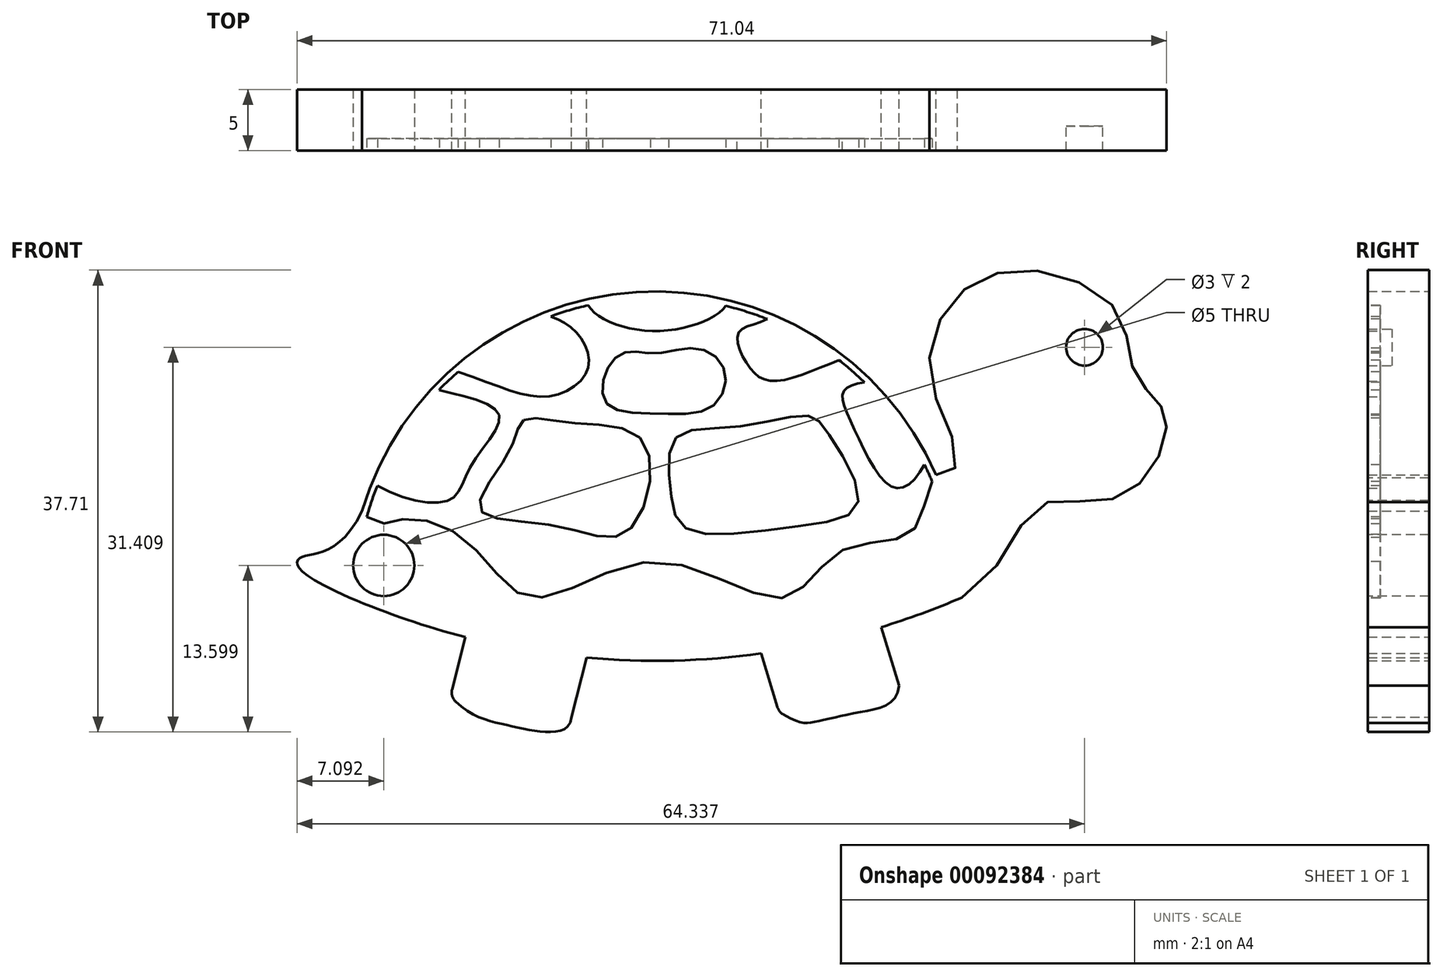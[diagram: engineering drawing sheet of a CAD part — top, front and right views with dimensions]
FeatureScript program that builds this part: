
annotation { "Feature Type Name" : "Feature", "Feature Type Description" : "" }
export const myFeature = defineFeature(function(context is Context, id is Id, definition is map)
    precondition{}
    {
        {
            var Q0;
            Q0=qCreatedBy(makeId("Front.planeOp"),FACE);
            var sketch = newSketch(context, id + "F0", { "sketchPlane" : qUnion([Q0])});
            skArc(sketch, "E0", {"start": v(25, 0) * mm, "mid": v(0, 25) * mm, "end": v(-25, 0) * mm});
            skArc(sketch, "E1", {"start": v(-25, 0) * mm, "mid": v(0, -5.16) * mm, "end": v(25, 0) * mm});
            skPoint(sketch, "E1.first.point", {"position": v(-25, 0) * mm});
            skPoint(sketch, "E1.second.point", {"position": v(25, 0) * mm});
            skArc(sketch, "E2", {"start": v(-22.9, 10.03) * mm, "mid": v(0, 4.84) * mm, "end": v(22.9, 10.03) * mm});
            skPoint(sketch, "E3.endSnap0", {"position": v(0, -5.16) * mm});
            skLineSegment(sketch, "E4", {"start": v(0, -5.16) * mm, "end": v(0, 14.84) * mm, "construction": true});
            skFitSpline(sketch, "E5.MirrorCS", {"points": [v(-22.9, 10.03) * mm, v(-28.86, 3.32) * mm, v(-25, 0) * mm], "startDerivative": vector(-9.95, -35.87) * mm, "endDerivative": vector(32.47, -14) * mm});
            skFitSpline(sketch, "E6", {"points": [v(22.9, 10.03) * mm, v(24.59, 11) * mm, v(22.49, 17.7) * mm, v(24.57, 24.55) * mm, v(30.78, 26.71) * mm, v(37.75, 23.3) * mm, v(39.05, 18.6) * mm, v(40.89, 16.14) * mm, v(41.74, 14.23) * mm, v(40.2, 10.04) * mm, v(36.08, 7.82) * mm, v(31.15, 7.38) * mm, v(25, 0) * mm], "startDerivative": vector(45.76, -39.88) * mm, "endDerivative": vector(-83.83, -36.13) * mm});
            skCircle(sketch, "E7", {"center": v(35.04, 20.44) * mm, "radius": 1.5 * mm});
            skArc(sketch, "E8", {"start": v(-24.41, 5.39) * mm, "mid": v(0, 0) * mm, "end": v(24.41, 5.39) * mm});
            skLineSegment(sketch, "E9", {"start": v(-15.53, -3.22) * mm, "end": v(-16.76, -8.07) * mm});
            skLineSegment(sketch, "E10", {"start": v(-6.87, -9.75) * mm, "end": v(-5.64, -4.9) * mm});
            skLineSegment(sketch, "E11", {"start": v(8.62, -4.57) * mm, "end": v(10.08, -9.35) * mm});
            skLineSegment(sketch, "E12", {"start": v(19.88, -7.2) * mm, "end": v(18.42, -2.41) * mm});
            skFitSpline(sketch, "E13", {"points": [v(-16.76, -8.07) * mm, v(-12.38, -10.35) * mm, v(-8.68, -10.97) * mm, v(-6.87, -9.75) * mm], "startDerivative": vector(11.77, -12.71) * mm, "endDerivative": vector(1.49, 11.94) * mm});
            skFitSpline(sketch, "E14", {"points": [v(10.08, -9.35) * mm, v(12.84, -10.18) * mm, v(16.55, -9.38) * mm, v(19.88, -7.2) * mm], "startDerivative": vector(16.48, -9.39) * mm, "endDerivative": vector(1.06, 14.58) * mm});
            skSolve(sketch);
        }
        {
            var Q0;
            Q0 = qSketchRegion(id + "F0", true);
            extrude(context, id + "F1", {"entities" : qUnion([Q0]), "depth" : 5 * mm});
        }
        {
            var Q0;
            Q0=makeQuery(id+"F1.opExtrude","CAP_FACE",FACE,{"disambiguationData":[OSD([sQuery(id+"F0.wireOp",EDGE,"E0"),sQuery(id+"F0.wireOp",EDGE,"E1"),sQuery(id+"F0.wireOp",EDGE,"E5.MirrorCS"),sQuery(id+"F0.wireOp",EDGE,"E6"),sQuery(id+"F0.wireOp",EDGE,"E7")])],"isStart":false});
            var sketch = newSketch(context, id + "F2", { "sketchPlane" : qUnion([Q0])});
            skFitSpline(sketch, "E15", {"points": [v(-5.68, 24.35) * mm, v(0, 21.77) * mm, v(5.98, 24.27) * mm], "startDerivative": vector(1.3, -8.7) * mm, "endDerivative": vector(2.25, 7.66) * mm});
            skFitSpline(sketch, "E16", {"points": [v(-16.68, 18.62) * mm, v(-8.69, 16.45) * mm, v(-5.54, 18.67) * mm, v(-6.45, 21.62) * mm, v(-9.3, 23.2) * mm], "startDerivative": vector(31.9, -10.33) * mm, "endDerivative": vector(-14.97, 4.58) * mm});
            skFitSpline(sketch, "E17", {"points": [v(-2.5, 20.03) * mm, v(0, 19.95) * mm, v(3.55, 20.33) * mm, v(5.67, 18.36) * mm, v(4.54, 15.56) * mm, v(0, 15.03) * mm, v(-3.95, 15.79) * mm, v(-4.1, 18.29) * mm, v(-2.5, 20.03) * mm]});
            skFitSpline(sketch, "E18", {"points": [v(9.62, 23.07) * mm, v(6.81, 21.7) * mm, v(7.5, 19.05) * mm, v(9.61, 17.68) * mm, v(15.54, 19.59) * mm], "startDerivative": vector(-11.22, -9.99) * mm, "endDerivative": vector(18.42, 6.43) * mm});
            skFitSpline(sketch, "E19", {"points": [v(-18.23, 17.1) * mm, v(-12.81, 14.95) * mm, v(-15.02, 10.87) * mm, v(-16.8, 8) * mm, v(-23.16, 9.4) * mm], "startDerivative": vector(21.71, -6.31) * mm, "endDerivative": vector(-23.28, 14.7) * mm});
            skFitSpline(sketch, "E20", {"points": [v(-10.77, 14.5) * mm, v(-11.9, 12.08) * mm, v(-14.36, 7.26) * mm, v(-8.1, 5.86) * mm, v(-2.27, 5.41) * mm, v(-0.92, 12.6) * mm, v(-6.98, 14.27) * mm, v(-10.77, 14.5) * mm]});
            skFitSpline(sketch, "E21", {"points": [v(1.66, 13.06) * mm, v(1.2, 8.88) * mm, v(2.52, 5.64) * mm, v(11.15, 5.78) * mm, v(16.53, 7.7) * mm, v(14.09, 13.44) * mm, v(12.48, 14.85) * mm, v(6.81, 13.97) * mm, v(1.66, 13.06) * mm]});
            skFitSpline(sketch, "E22", {"points": [v(17.74, 17.62) * mm, v(15.37, 16.85) * mm, v(16.13, 13.97) * mm, v(19.56, 8.95) * mm, v(22.23, 11.43) * mm], "startDerivative": vector(-16.1, -0.64) * mm, "endDerivative": vector(7.34, 17.47) * mm});
            skFitSpline(sketch, "E23", {"points": [v(-23.98, 7.06) * mm, v(-21.05, 6.35) * mm, v(-15.5, 4.69) * mm, v(-10.18, 0) * mm, v(0, 2.93) * mm, v(10.5, 0) * mm, v(15.13, 3.82) * mm, v(20.84, 5.3) * mm, v(22.9, 10.03) * mm], "startDerivative": vector(41.64, -57.43) * mm, "endDerivative": vector(26.72, 40.4) * mm});
            skArc(sketch, "E24", {"start": v(-23.98, 7.06) * mm, "mid": v(-1.58, 24.95) * mm, "end": v(22.9, 10.03) * mm});
            skArc(sketch, "E25", {"start": v(-23.6, 6.6) * mm, "mid": v(-1.52, 24.45) * mm, "end": v(22.6, 9.47) * mm});
            skSolve(sketch);
        }
        {
            var Q0;
            Q0=makeQuery(id+"F2.imprint","IMPRINT",FACE,{"disambiguationData":[TD([[makeQuery(id+"F2.imprint","IMPRINT",EDGE,{"derivedFrom":sQuery(id+"F2.wireOp",EDGE,"E17")}),1.0]])]});
            extrude(context, id + "F3", {"entities" : qUnion([Q0]), "operationType" : NewBodyOperationType.REMOVE, "oppositeDirection" : true, "depth" : 1 * mm});
        }
        {
            var Q0;
            Q0=makeQuery(id+"F1.opExtrude","SWEPT_EDGE",EDGE,{"disambiguationData":[OSD([sQuery(id+"F0.wireOp",EDGE,"E9"),sQuery(id+"F0.wireOp",EDGE,"E13")])]});
            var Q1;
            Q1=makeQuery(id+"F1.opExtrude","SWEPT_EDGE",EDGE,{"disambiguationData":[OSD([sQuery(id+"F0.wireOp",EDGE,"E11"),sQuery(id+"F0.wireOp",EDGE,"E14")])]});
            fillet(context, id + "F4", {"entities" : qUnion([Q0, Q1]), "radius" : 1 * mm, "tangentPropagation" : true, "allowEdgeOverflow" : false});
        }
        {
            var Q0;
            Q0=makeQuery(id+"F0.imprint","IMPRINT",FACE,{"disambiguationData":[TD([[makeQuery(id+"F0.imprint","IMPRINT",EDGE,{"derivedFrom":sQuery(id+"F0.wireOp",EDGE,"E7")}),1.0]])]});
            extrude(context, id + "F5", {"entities" : qUnion([Q0]), "operationType" : NewBodyOperationType.ADD, "depth" : 3 * mm});
        }
        {
            var Q0;
            {var subQ3=sQuery(id+"F0.wireOp",EDGE,"E10");var subQ4=sQuery(id+"F0.wireOp",EDGE,"E1");var subQ5=sQuery(id+"F0.wireOp",EDGE,"E11");var subQ7=sQuery(id+"F0.wireOp",EDGE,"E6");var subQ10=sQuery(id+"F0.wireOp",EDGE,"E5.MirrorCS");var subQ11=sQuery(id+"F0.wireOp",EDGE,"E0");var subQ12=sQuery(id+"F0.wireOp",EDGE,"E9");var subQ13=sQuery(id+"F0.wireOp",EDGE,"E14");var subQ14=sQuery(id+"F0.wireOp",EDGE,"E13");var subQ15=sQuery(id+"F0.wireOp",EDGE,"E12");var subQ17=sQuery(id+"F0.wireOp",EDGE,"E7");Q0=makeQuery(id+"F3.boolean.opBoolean","SPLIT",FACE,{"disambiguationData":[TD([makeQuery(id+"F1.opExtrude","SWEPT_FACE",FACE,{"disambiguationData":[OSD([subQ11])]})])],"derivedFrom":makeQuery(id+"F1.opExtrude","CAP_FACE",FACE,{"disambiguationData":[OSD([subQ11,subQ4,subQ10,subQ7,subQ17,subQ12,subQ3,subQ5,subQ15,subQ14,subQ13])],"isStart":false})});}
            var sketch = newSketch(context, id + "F6", { "sketchPlane" : qUnion([Q0])});
            skCircle(sketch, "E26", {"center": v(-22.2, 2.63) * mm, "radius": 2.5 * mm});
            skSolve(sketch);
        }
        {
            var Q0;
            Q0 = qSketchRegion(id + "F6", true);
            extrude(context, id + "F7", {"entities" : qUnion([Q0]), "operationType" : NewBodyOperationType.REMOVE, "endBound" : BoundingType.THROUGH_ALL, "oppositeDirection" : true, "depth" : 25 * mm});
        }
    });
